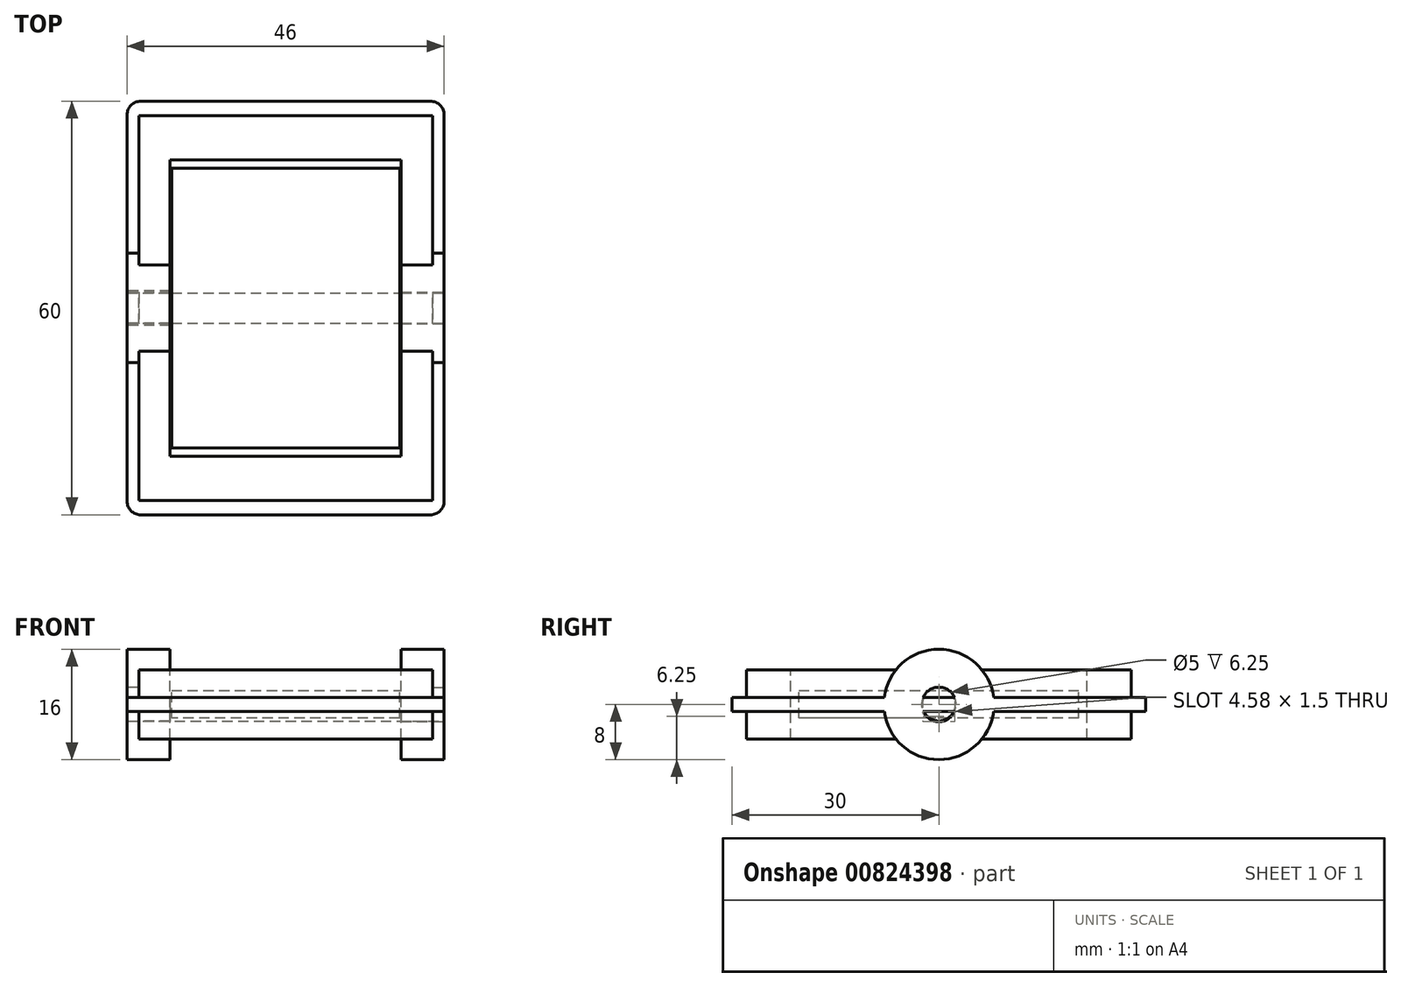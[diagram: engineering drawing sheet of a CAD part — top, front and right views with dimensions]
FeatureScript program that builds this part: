
annotation { "Feature Type Name" : "Feature", "Feature Type Description" : "" }
export const myFeature = defineFeature(function(context is Context, id is Id, definition is map)
    precondition{}
    {
        {
            var Q0;
            Q0=qCreatedBy(makeId("Top.planeOp"),FACE);
            var sketch = newSketch(context, id + "F0", { "sketchPlane" : qUnion([Q0])});
            skLineSegment(sketch, "E0.bottom", {"start": v(-40.6, 30) * mm, "end": v(5.4, 30) * mm});
            skLineSegment(sketch, "E0.left", {"start": v(-40.6, 30) * mm, "end": v(-40.6, 0) * mm});
            skLineSegment(sketch, "E0.right", {"start": v(5.4, 30) * mm, "end": v(5.4, 0) * mm});
            skLineSegment(sketch, "E1.MirrorCS", {"start": v(-40.6, -30) * mm, "end": v(-40.6, 0) * mm});
            skLineSegment(sketch, "E2.MirrorCS", {"start": v(-40.6, -30) * mm, "end": v(5.4, -30) * mm});
            skLineSegment(sketch, "E3.MirrorCS", {"start": v(5.4, -30) * mm, "end": v(5.4, 0) * mm});
            skSolve(sketch);
        }
        {
            var Q0;
            Q0 = qSketchRegion(id + "F0", true);
            extrude(context, id + "F1", {"entities" : qUnion([Q0]), "depth" : 6 * mm, "offsetDistance" : 25 * mm});
        }
        {
            var Q0;
            Q0=makeQuery(id+"F1.opExtrude","CAP_FACE",FACE,{"disambiguationData":[OSD([sQuery(id+"F0.wireOp",EDGE,"E0.bottom"),sQuery(id+"F0.wireOp",EDGE,"E0.left"),sQuery(id+"F0.wireOp",EDGE,"E0.right"),sQuery(id+"F0.wireOp",EDGE,"E1.MirrorCS"),sQuery(id+"F0.wireOp",EDGE,"E2.MirrorCS"),sQuery(id+"F0.wireOp",EDGE,"E3.MirrorCS")])],"isStart":false});
            var sketch = newSketch(context, id + "F2", { "sketchPlane" : qUnion([Q0])});
            skLineSegment(sketch, "E4.bottom", {"start": v(-38.9, 27.9) * mm, "end": v(3.7, 27.9) * mm});
            skLineSegment(sketch, "E4.top", {"start": v(-38.9, -27.9) * mm, "end": v(3.7, -27.9) * mm});
            skLineSegment(sketch, "E4.left", {"start": v(-38.9, 27.9) * mm, "end": v(-38.9, -27.9) * mm});
            skLineSegment(sketch, "E4.right", {"start": v(3.7, 27.9) * mm, "end": v(3.7, -27.9) * mm});
            skLineSegment(sketch, "E5.0", {"start": v(-40.6, 30) * mm, "end": v(5.4, 30) * mm});
            skLineSegment(sketch, "E6.0", {"start": v(-40.6, 30) * mm, "end": v(-40.6, -30) * mm});
            skLineSegment(sketch, "E7.0", {"start": v(-40.6, -30) * mm, "end": v(5.4, -30) * mm});
            skLineSegment(sketch, "E8.0", {"start": v(5.4, -30) * mm, "end": v(5.4, 30) * mm});
            skSolve(sketch);
        }
        {
            var Q0;
            Q0 = qSketchRegion(id + "F2", true);
            extrude(context, id + "F3", {"entities" : qUnion([Q0]), "operationType" : NewBodyOperationType.REMOVE, "oppositeDirection" : true, "depth" : 4 * mm, "offsetDistance" : 25 * mm});
        }
        {
            var Q0;
            Q0=makeQuery(id+"F1.opExtrude","SWEPT_EDGE",EDGE,{"disambiguationData":[OSD([sQuery(id+"F0.wireOp",EDGE,"E2.MirrorCS"),sQuery(id+"F0.wireOp",EDGE,"E3.MirrorCS")])]});
            cPlane(context, id + "F4", {"entities" : qUnion([Q0]), "cplaneType" : CPlaneType.MID_PLANE, "offset" : 25 * mm, "width" : 150 * mm, "height" : 150 * mm});
        }
        {
            var Q0;
            Q0=makeQuery(id+"F1.opExtrude","SWEPT_BODY",BODY,{"disambiguationData":[OSD([sQuery(id+"F0.wireOp",EDGE,"E0.bottom"),sQuery(id+"F0.wireOp",EDGE,"E0.left"),sQuery(id+"F0.wireOp",EDGE,"E0.right"),sQuery(id+"F0.wireOp",EDGE,"E1.MirrorCS"),sQuery(id+"F0.wireOp",EDGE,"E2.MirrorCS"),sQuery(id+"F0.wireOp",EDGE,"E3.MirrorCS")])]});
            var Q1;
            Q1=qCreatedBy(id+"F4.planeOp",FACE);
            mirror(context, id + "F5", {"operationType" : NewBodyOperationType.ADD, "entities" : qUnion([Q0]), "mirrorPlane" : qUnion([Q1])});
        }
        {
            var Q0;
            Q0=makeQuery(id+"F1.opExtrude","SWEPT_EDGE",EDGE,{"disambiguationData":[OSD([sQuery(id+"F0.wireOp",EDGE,"E0.bottom"),sQuery(id+"F0.wireOp",EDGE,"E0.left")])]});
            var Q1;
            Q1=makeQuery(id+"F1.opExtrude","SWEPT_EDGE",EDGE,{"disambiguationData":[OSD([sQuery(id+"F0.wireOp",EDGE,"E0.bottom"),sQuery(id+"F0.wireOp",EDGE,"E0.right")])]});
            var Q2;
            Q2=makeQuery(id+"F1.opExtrude","SWEPT_EDGE",EDGE,{"disambiguationData":[OSD([sQuery(id+"F0.wireOp",EDGE,"E2.MirrorCS"),sQuery(id+"F0.wireOp",EDGE,"E3.MirrorCS")])]});
            var Q3;
            Q3=makeQuery(id+"F1.opExtrude","SWEPT_EDGE",EDGE,{"disambiguationData":[OSD([sQuery(id+"F0.wireOp",EDGE,"E1.MirrorCS"),sQuery(id+"F0.wireOp",EDGE,"E2.MirrorCS")])]});
            fillet(context, id + "F6", {"entities" : qUnion([Q0, Q1, Q2, Q3]), "radius" : 2 * mm, "tangentPropagation" : true, "allowEdgeOverflow" : false});
        }
        {
            var Q0;
            Q0=makeQuery(id+"F1.opExtrude","CAP_FACE",FACE,{"disambiguationData":[OSD([sQuery(id+"F0.wireOp",EDGE,"E0.bottom"),sQuery(id+"F0.wireOp",EDGE,"E0.left"),sQuery(id+"F0.wireOp",EDGE,"E0.right"),sQuery(id+"F0.wireOp",EDGE,"E1.MirrorCS"),sQuery(id+"F0.wireOp",EDGE,"E2.MirrorCS"),sQuery(id+"F0.wireOp",EDGE,"E3.MirrorCS")])],"isStart":false});
            var sketch = newSketch(context, id + "F7", { "sketchPlane" : qUnion([Q0])});
            skLineSegment(sketch, "E9.bottom", {"start": v(-34.35, -21.5) * mm, "end": v(-0.85, -21.5) * mm});
            skLineSegment(sketch, "E9.top", {"start": v(-34.35, 21.5) * mm, "end": v(-0.85, 21.5) * mm});
            skLineSegment(sketch, "E9.left", {"start": v(-34.35, -21.5) * mm, "end": v(-34.35, 21.5) * mm});
            skLineSegment(sketch, "E9.right", {"start": v(-0.85, -21.5) * mm, "end": v(-0.85, 21.5) * mm});
            skLineSegment(sketch, "E10.0", {"start": v(-38.9, 27.9) * mm, "end": v(-38.9, -27.9) * mm});
            skLineSegment(sketch, "E11.0", {"start": v(-38.9, -27.9) * mm, "end": v(3.7, -27.9) * mm});
            skLineSegment(sketch, "E12.bottom", {"start": v(-34.15, -20.3) * mm, "end": v(-1.05, -20.3) * mm});
            skLineSegment(sketch, "E12.top", {"start": v(-34.15, 20.3) * mm, "end": v(-1.05, 20.3) * mm});
            skLineSegment(sketch, "E12.left", {"start": v(-34.15, -20.3) * mm, "end": v(-34.15, 20.3) * mm});
            skLineSegment(sketch, "E12.right", {"start": v(-1.05, -20.3) * mm, "end": v(-1.05, 20.3) * mm});
            skSolve(sketch);
        }
        {
            var Q0;
            Q0 = qSketchRegion(id + "F7", true);
            extrude(context, id + "F8", {"entities" : qUnion([Q0]), "operationType" : NewBodyOperationType.REMOVE, "oppositeDirection" : true, "depth" : 25 * mm, "offsetDistance" : 25 * mm});
        }
        {
            var Q0;
            Q0=makeQuery(id+"F8.boolean.opBoolean","SPLIT",FACE,{"disambiguationData":[TD([makeQuery(id+"F8.opExtrude","SWEPT_FACE",FACE,{"disambiguationData":[OSD([sQuery(id+"F7.wireOp",EDGE,"E12.bottom")])]})])],"derivedFrom":makeQuery(id+"F1.opExtrude","CAP_FACE",FACE,{"disambiguationData":[OSD([sQuery(id+"F0.wireOp",EDGE,"E0.bottom"),sQuery(id+"F0.wireOp",EDGE,"E0.left"),sQuery(id+"F0.wireOp",EDGE,"E0.right"),sQuery(id+"F0.wireOp",EDGE,"E1.MirrorCS"),sQuery(id+"F0.wireOp",EDGE,"E2.MirrorCS"),sQuery(id+"F0.wireOp",EDGE,"E3.MirrorCS")])],"isStart":false})});
            var Q1;
            Q1=makeQuery(id+"F8.boolean.opBoolean","SPLIT",FACE,{"disambiguationData":[TD([makeQuery(id+"F8.opExtrude","SWEPT_FACE",FACE,{"disambiguationData":[OSD([sQuery(id+"F7.wireOp",EDGE,"E12.bottom")])]})])],"derivedFrom":makeQuery(id+"F5.opPattern","COPY",FACE,{"derivedFrom":makeQuery(id+"F1.opExtrude","CAP_FACE",FACE,{"disambiguationData":[OSD([sQuery(id+"F0.wireOp",EDGE,"E0.bottom"),sQuery(id+"F0.wireOp",EDGE,"E0.left"),sQuery(id+"F0.wireOp",EDGE,"E0.right"),sQuery(id+"F0.wireOp",EDGE,"E1.MirrorCS"),sQuery(id+"F0.wireOp",EDGE,"E2.MirrorCS"),sQuery(id+"F0.wireOp",EDGE,"E3.MirrorCS")])],"isStart":false}),"instanceName":"1"})});
            extrude(context, id + "F9", {"entities" : qUnion([Q0, Q1]), "operationType" : NewBodyOperationType.REMOVE, "oppositeDirection" : true, "depth" : 3 * mm, "offsetDistance" : 25 * mm});
        }
        {
            var Q0;
            Q0=makeQuery(id+"F8.boolean.opBoolean","SPLIT",FACE,{"disambiguationData":[TD([makeQuery(id+"F8.opExtrude","SWEPT_FACE",FACE,{"disambiguationData":[OSD([sQuery(id+"F7.wireOp",EDGE,"E12.bottom")])]})])],"derivedFrom":makeQuery(id+"F5.opPattern","COPY",FACE,{"derivedFrom":makeQuery(id+"F1.opExtrude","CAP_FACE",FACE,{"disambiguationData":[OSD([sQuery(id+"F0.wireOp",EDGE,"E0.bottom"),sQuery(id+"F0.wireOp",EDGE,"E0.left"),sQuery(id+"F0.wireOp",EDGE,"E0.right"),sQuery(id+"F0.wireOp",EDGE,"E1.MirrorCS"),sQuery(id+"F0.wireOp",EDGE,"E2.MirrorCS"),sQuery(id+"F0.wireOp",EDGE,"E3.MirrorCS")])],"isStart":false}),"instanceName":"1"})});
            extrude(context, id + "F10", {"entities" : qUnion([Q0]), "operationType" : NewBodyOperationType.REMOVE, "oppositeDirection" : true, "depth" : 3 * mm, "offsetDistance" : 25 * mm});
        }
        {
            var Q0;
            Q0=makeQuery(id+"F1.opExtrude","SWEPT_FACE",FACE,{"disambiguationData":[OSD([sQuery(id+"F0.wireOp",EDGE,"E0.right"),sQuery(id+"F0.wireOp",EDGE,"E3.MirrorCS")])]});
            var sketch = newSketch(context, id + "F11", { "sketchPlane" : qUnion([Q0])});
            skCircle(sketch, "E13", {"center": v(0, 1) * mm, "radius": 8 * mm});
            skCircle(sketch, "E14", {"center": v(0, 1) * mm, "radius": 2.5 * mm});
            skCircle(sketch, "E15", {"center": v(0, 1) * mm, "radius": 2.4 * mm});
            skSolve(sketch);
        }
        {
            var Q0;
            Q0 = qSketchRegion(id + "F11", true);
            var Q1;
            {var subQ0=sQuery(id+"F11.wireOp",EDGE,"E15");var subQ1=makeQuery(id+"F1.opExtrude","CAP_EDGE",EDGE,{"disambiguationData":[OSD([sQuery(id+"F0.wireOp",EDGE,"E0.right"),sQuery(id+"F0.wireOp",EDGE,"E3.MirrorCS")])],"isStart":true});var subQ2=makeQuery(id+"F11.imprint","INTERSECT",VERTEX,{"disambiguationData":[OD(0.0)],"derivedFrom":[subQ1,subQ0]});Q1=makeQuery(id+"F11.imprint","IMPRINT",FACE,{"disambiguationData":[TD([[makeQuery(id+"F11.imprint","IMPRINT",EDGE,{"disambiguationData":[TD([[subQ2,-1.0]])],"derivedFrom":subQ0}),1.0]])]});}
            var Q2;
            {var subQ0=sQuery(id+"F11.wireOp",EDGE,"E15");var subQ1=makeQuery(id+"F3.boolean.opBoolean","COPY",EDGE,{"derivedFrom":makeQuery(id+"F3.opExtrude","CAP_EDGE",EDGE,{"disambiguationData":[OSD([sQuery(id+"F2.wireOp",EDGE,"E8.0")])],"isStart":false})});var subQ2=makeQuery(id+"F11.imprint","INTERSECT",VERTEX,{"disambiguationData":[OD(0.0)],"derivedFrom":[subQ1,subQ0]});Q2=makeQuery(id+"F11.imprint","IMPRINT",FACE,{"disambiguationData":[TD([[makeQuery(id+"F11.imprint","IMPRINT",EDGE,{"disambiguationData":[TD([[subQ2,-1.0]])],"derivedFrom":subQ1}),-1.0]])]});}
            var Q3;
            {var subQ0=sQuery(id+"F11.wireOp",EDGE,"E15");var subQ1=makeQuery(id+"F3.boolean.opBoolean","COPY",EDGE,{"derivedFrom":makeQuery(id+"F3.opExtrude","CAP_EDGE",EDGE,{"disambiguationData":[OSD([sQuery(id+"F2.wireOp",EDGE,"E8.0")])],"isStart":false})});var subQ2=makeQuery(id+"F11.imprint","INTERSECT",VERTEX,{"disambiguationData":[OD(0.0)],"derivedFrom":[subQ1,subQ0]});Q3=makeQuery(id+"F11.imprint","IMPRINT",FACE,{"disambiguationData":[TD([[makeQuery(id+"F11.imprint","IMPRINT",EDGE,{"disambiguationData":[TD([[subQ2,1.0]])],"derivedFrom":subQ0}),1.0]])]});}
            extrude(context, id + "F12", {"entities" : qUnion([Q0, Q1, Q2, Q3]), "oppositeDirection" : true, "depth" : 6.25 * mm, "offsetDistance" : 25 * mm});
        }
        {
            var Q0;
            {var subQ0=sQuery(id+"F11.wireOp",EDGE,"E14");var subQ1=makeQuery(id+"F3.boolean.opBoolean","COPY",EDGE,{"derivedFrom":makeQuery(id+"F3.opExtrude","CAP_EDGE",EDGE,{"disambiguationData":[OSD([sQuery(id+"F2.wireOp",EDGE,"E8.0")])],"isStart":false})});var subQ2=makeQuery(id+"F11.imprint","INTERSECT",VERTEX,{"disambiguationData":[OD(0.0)],"derivedFrom":[subQ1,subQ0]});Q0=makeQuery(id+"F11.imprint","IMPRINT",FACE,{"disambiguationData":[TD([[makeQuery(id+"F11.imprint","IMPRINT",EDGE,{"disambiguationData":[TD([[subQ2,-1.0]])],"derivedFrom":subQ1}),-1.0]])]});}
            var Q1;
            {var subQ0=sQuery(id+"F11.wireOp",EDGE,"E14");var subQ1=makeQuery(id+"F3.boolean.opBoolean","COPY",EDGE,{"derivedFrom":makeQuery(id+"F3.opExtrude","CAP_EDGE",EDGE,{"disambiguationData":[OSD([sQuery(id+"F2.wireOp",EDGE,"E8.0")])],"isStart":false})});var subQ2=makeQuery(id+"F11.imprint","INTERSECT",VERTEX,{"disambiguationData":[OD(0.0)],"derivedFrom":[subQ1,subQ0]});Q1=makeQuery(id+"F11.imprint","IMPRINT",FACE,{"disambiguationData":[TD([[makeQuery(id+"F11.imprint","IMPRINT",EDGE,{"disambiguationData":[TD([[subQ2,1.0]])],"derivedFrom":subQ0}),1.0]])]});}
            var Q2;
            {var subQ0=sQuery(id+"F11.wireOp",EDGE,"E14");var subQ1=makeQuery(id+"F1.opExtrude","CAP_EDGE",EDGE,{"disambiguationData":[OSD([sQuery(id+"F0.wireOp",EDGE,"E0.right"),sQuery(id+"F0.wireOp",EDGE,"E3.MirrorCS")])],"isStart":true});var subQ2=makeQuery(id+"F11.imprint","INTERSECT",VERTEX,{"disambiguationData":[OD(0.0)],"derivedFrom":[subQ1,subQ0]});Q2=makeQuery(id+"F11.imprint","IMPRINT",FACE,{"disambiguationData":[TD([[makeQuery(id+"F11.imprint","IMPRINT",EDGE,{"disambiguationData":[TD([[subQ2,-1.0]])],"derivedFrom":subQ0}),1.0]])]});}
            var Q3;
            {var subQ0=sQuery(id+"F11.wireOp",EDGE,"E14");var subQ1=makeQuery(id+"F3.boolean.opBoolean","COPY",EDGE,{"derivedFrom":makeQuery(id+"F3.opExtrude","CAP_EDGE",EDGE,{"disambiguationData":[OSD([sQuery(id+"F2.wireOp",EDGE,"E8.0")])],"isStart":false})});var subQ2=makeQuery(id+"F11.imprint","INTERSECT",VERTEX,{"disambiguationData":[OD(1.0)],"derivedFrom":[subQ1,subQ0]});Q3=makeQuery(id+"F11.imprint","IMPRINT",FACE,{"disambiguationData":[TD([[makeQuery(id+"F11.imprint","IMPRINT",EDGE,{"disambiguationData":[TD([[subQ2,1.0]])],"derivedFrom":subQ1}),-1.0]])]});}
            extrude(context, id + "F13", {"entities" : qUnion([Q0, Q1, Q2, Q3]), "operationType" : NewBodyOperationType.REMOVE, "oppositeDirection" : true, "depth" : 6.25 * mm, "offsetDistance" : 25 * mm});
        }
        {
            var Q0;
            {var subQ0=sQuery(id+"F11.wireOp",EDGE,"E15");var subQ1=makeQuery(id+"F3.boolean.opBoolean","COPY",EDGE,{"derivedFrom":makeQuery(id+"F3.opExtrude","CAP_EDGE",EDGE,{"disambiguationData":[OSD([sQuery(id+"F2.wireOp",EDGE,"E8.0")])],"isStart":false})});var subQ2=makeQuery(id+"F11.imprint","INTERSECT",VERTEX,{"disambiguationData":[OD(0.0)],"derivedFrom":[subQ1,subQ0]});Q0=makeQuery(id+"F11.imprint","IMPRINT",FACE,{"disambiguationData":[TD([[makeQuery(id+"F11.imprint","IMPRINT",EDGE,{"disambiguationData":[TD([[subQ2,-1.0]])],"derivedFrom":subQ1}),-1.0]])]});}
            var Q1;
            {var subQ0=sQuery(id+"F11.wireOp",EDGE,"E15");var subQ1=makeQuery(id+"F3.boolean.opBoolean","COPY",EDGE,{"derivedFrom":makeQuery(id+"F3.opExtrude","CAP_EDGE",EDGE,{"disambiguationData":[OSD([sQuery(id+"F2.wireOp",EDGE,"E8.0")])],"isStart":false})});var subQ2=makeQuery(id+"F11.imprint","INTERSECT",VERTEX,{"disambiguationData":[OD(0.0)],"derivedFrom":[subQ1,subQ0]});Q1=makeQuery(id+"F11.imprint","IMPRINT",FACE,{"disambiguationData":[TD([[makeQuery(id+"F11.imprint","IMPRINT",EDGE,{"disambiguationData":[TD([[subQ2,1.0]])],"derivedFrom":subQ0}),1.0]])]});}
            var Q2;
            {var subQ0=sQuery(id+"F11.wireOp",EDGE,"E15");var subQ1=makeQuery(id+"F1.opExtrude","CAP_EDGE",EDGE,{"disambiguationData":[OSD([sQuery(id+"F0.wireOp",EDGE,"E0.right"),sQuery(id+"F0.wireOp",EDGE,"E3.MirrorCS")])],"isStart":true});var subQ2=makeQuery(id+"F11.imprint","INTERSECT",VERTEX,{"disambiguationData":[OD(0.0)],"derivedFrom":[subQ1,subQ0]});Q2=makeQuery(id+"F11.imprint","IMPRINT",FACE,{"disambiguationData":[TD([[makeQuery(id+"F11.imprint","IMPRINT",EDGE,{"disambiguationData":[TD([[subQ2,-1.0]])],"derivedFrom":subQ0}),1.0]])]});}
            extrude(context, id + "F14", {"entities" : qUnion([Q0, Q1, Q2]), "oppositeDirection" : true, "depth" : 46 * mm, "offsetDistance" : 25 * mm});
        }
        {
            var Q0;
            Q0=makeQuery(id+"F8.boolean.opBoolean","COPY",FACE,{"derivedFrom":makeQuery(id+"F8.opExtrude","SWEPT_FACE",FACE,{"disambiguationData":[OSD([sQuery(id+"F7.wireOp",EDGE,"E12.left")])]})});
            var Q1;
            Q1=makeQuery(id+"F8.boolean.opBoolean","COPY",FACE,{"derivedFrom":makeQuery(id+"F8.opExtrude","SWEPT_FACE",FACE,{"disambiguationData":[OSD([sQuery(id+"F7.wireOp",EDGE,"E12.right")])]})});
            cPlane(context, id + "F15", {"entities" : qUnion([Q0, Q1]), "cplaneType" : CPlaneType.MID_PLANE, "offset" : 25 * mm, "width" : 150 * mm, "height" : 150 * mm});
        }
        {
            var Q0;
            Q0=makeQuery(id+"F12.opExtrude","SWEPT_BODY",BODY,{"disambiguationData":[OSD([sQuery(id+"F11.wireOp",EDGE,"E13"),sQuery(id+"F11.wireOp",EDGE,"E14")])]});
            var Q1;
            Q1=qCreatedBy(id+"F15.planeOp",FACE);
            mirror(context, id + "F16", {"operationType" : NewBodyOperationType.ADD, "entities" : qUnion([Q0]), "mirrorPlane" : qUnion([Q1])});
        }
        {
            var Q0;
            Q0=makeQuery(id+"F16.boolean.opBoolean","MERGE",FACE,{"derivedFrom":[makeQuery(id+"F1.opExtrude","SWEPT_FACE",FACE,{"disambiguationData":[OSD([sQuery(id+"F0.wireOp",EDGE,"E0.left"),sQuery(id+"F0.wireOp",EDGE,"E1.MirrorCS")])]}),makeQuery(id+"F16.opPattern","COPY",FACE,{"derivedFrom":makeQuery(id+"F12.opExtrude","CAP_FACE",FACE,{"disambiguationData":[OSD([sQuery(id+"F11.wireOp",EDGE,"E13"),sQuery(id+"F11.wireOp",EDGE,"E14")])],"isStart":true}),"instanceName":"1"})]});
            var sketch = newSketch(context, id + "F17", { "sketchPlane" : qUnion([Q0])});
            skCircle(sketch, "E16.0", {"center": v(0, 1) * mm, "radius": 2.4 * mm});
            skCircle(sketch, "E17", {"center": v(0, 1) * mm, "radius": 2.5 * mm});
            skSolve(sketch);
        }
        {
            var Q0;
            {var subQ0=sQuery(id+"F17.wireOp",EDGE,"E16.0");var subQ1=sQuery(id+"F0.wireOp",EDGE,"E1.MirrorCS");var subQ2=sQuery(id+"F0.wireOp",EDGE,"E0.left");var subQ5=sQuery(id+"F11.wireOp",EDGE,"E14");var subQ7=makeQuery(id+"F16.opPattern","COPY",FACE,{"derivedFrom":makeQuery(id+"F12.opExtrude","SWEPT_FACE",FACE,{"disambiguationData":[OSD([subQ5])]}),"instanceName":"1"});var subQ10=makeQuery(id+"F16.boolean.opBoolean","SPLIT",EDGE,{"disambiguationData":[TD([subQ7])],"derivedFrom":makeQuery(id+"F1.opExtrude","CAP_EDGE",EDGE,{"disambiguationData":[OSD([subQ2,subQ1])],"isStart":true})});var subQ11=makeQuery(id+"F17.imprint","INTERSECT",VERTEX,{"disambiguationData":[OD(0.0)],"derivedFrom":[subQ10,subQ0]});Q0=makeQuery(id+"F17.imprint","IMPRINT",FACE,{"disambiguationData":[TD([[makeQuery(id+"F17.imprint","IMPRINT",EDGE,{"disambiguationData":[TD([[subQ11,1.0]])],"derivedFrom":subQ0}),-1.0]])]});}
            var Q1;
            {var subQ0=sQuery(id+"F17.wireOp",EDGE,"E16.0");var subQ1=sQuery(id+"F0.wireOp",EDGE,"E1.MirrorCS");var subQ2=sQuery(id+"F0.wireOp",EDGE,"E0.left");var subQ5=sQuery(id+"F11.wireOp",EDGE,"E14");var subQ7=makeQuery(id+"F16.opPattern","COPY",FACE,{"derivedFrom":makeQuery(id+"F12.opExtrude","SWEPT_FACE",FACE,{"disambiguationData":[OSD([subQ5])]}),"instanceName":"1"});var subQ10=makeQuery(id+"F16.boolean.opBoolean","SPLIT",EDGE,{"disambiguationData":[TD([subQ7])],"derivedFrom":makeQuery(id+"F1.opExtrude","CAP_EDGE",EDGE,{"disambiguationData":[OSD([subQ2,subQ1])],"isStart":true})});var subQ11=makeQuery(id+"F17.imprint","INTERSECT",VERTEX,{"disambiguationData":[OD(1.0)],"derivedFrom":[subQ10,subQ0]});Q1=makeQuery(id+"F17.imprint","IMPRINT",FACE,{"disambiguationData":[TD([[makeQuery(id+"F17.imprint","IMPRINT",EDGE,{"disambiguationData":[TD([[subQ11,-1.0]])],"derivedFrom":subQ0}),-1.0]])]});}
            var Q2;
            {var subQ0=sQuery(id+"F17.wireOp",EDGE,"E16.0");var subQ1=sQuery(id+"F2.wireOp",EDGE,"E6.0");var subQ2=sQuery(id+"F11.wireOp",EDGE,"E14");var subQ3=makeQuery(id+"F16.boolean.opBoolean","SPLIT",EDGE,{"disambiguationData":[TD([makeQuery(id+"F16.opPattern","COPY",FACE,{"derivedFrom":makeQuery(id+"F12.opExtrude","SWEPT_FACE",FACE,{"disambiguationData":[OSD([subQ2])]}),"instanceName":"1"})])],"derivedFrom":makeQuery(id+"F3.boolean.opBoolean","COPY",EDGE,{"derivedFrom":makeQuery(id+"F3.opExtrude","CAP_EDGE",EDGE,{"disambiguationData":[OSD([subQ1])],"isStart":false})})});var subQ4=makeQuery(id+"F17.imprint","INTERSECT",VERTEX,{"disambiguationData":[OD(0.0)],"derivedFrom":[subQ3,subQ0]});Q2=makeQuery(id+"F17.imprint","IMPRINT",FACE,{"disambiguationData":[TD([[makeQuery(id+"F17.imprint","IMPRINT",EDGE,{"disambiguationData":[TD([[subQ4,1.0]])],"derivedFrom":subQ0}),-1.0]])]});}
            var Q3;
            {var subQ0=sQuery(id+"F17.wireOp",EDGE,"E16.0");var subQ1=sQuery(id+"F0.wireOp",EDGE,"E1.MirrorCS");var subQ2=sQuery(id+"F0.wireOp",EDGE,"E0.left");var subQ3=sQuery(id+"F11.wireOp",EDGE,"E14");var subQ4=makeQuery(id+"F16.boolean.opBoolean","SPLIT",EDGE,{"disambiguationData":[TD([makeQuery(id+"F16.opPattern","COPY",FACE,{"derivedFrom":makeQuery(id+"F12.opExtrude","SWEPT_FACE",FACE,{"disambiguationData":[OSD([subQ3])]}),"instanceName":"1"})])],"derivedFrom":makeQuery(id+"F1.opExtrude","CAP_EDGE",EDGE,{"disambiguationData":[OSD([subQ2,subQ1])],"isStart":true})});var subQ5=makeQuery(id+"F17.imprint","INTERSECT",VERTEX,{"disambiguationData":[OD(0.0)],"derivedFrom":[subQ4,subQ0]});Q3=makeQuery(id+"F17.imprint","IMPRINT",FACE,{"disambiguationData":[TD([[makeQuery(id+"F17.imprint","IMPRINT",EDGE,{"disambiguationData":[TD([[subQ5,-1.0]])],"derivedFrom":subQ0}),-1.0]])]});}
            extrude(context, id + "F18", {"entities" : qUnion([Q0, Q1, Q2, Q3]), "operationType" : NewBodyOperationType.REMOVE, "oppositeDirection" : true, "depth" : 6.25 * mm, "offsetDistance" : 25 * mm});
        }
        {
            var Q0;
            Q0=makeQuery(id+"F12.opExtrude","SWEPT_BODY",BODY,{"disambiguationData":[OSD([sQuery(id+"F11.wireOp",EDGE,"E15")])]});
            deleteBodies(context, id + "F19", {"entities" : qUnion([Q0])});
        }
    });
